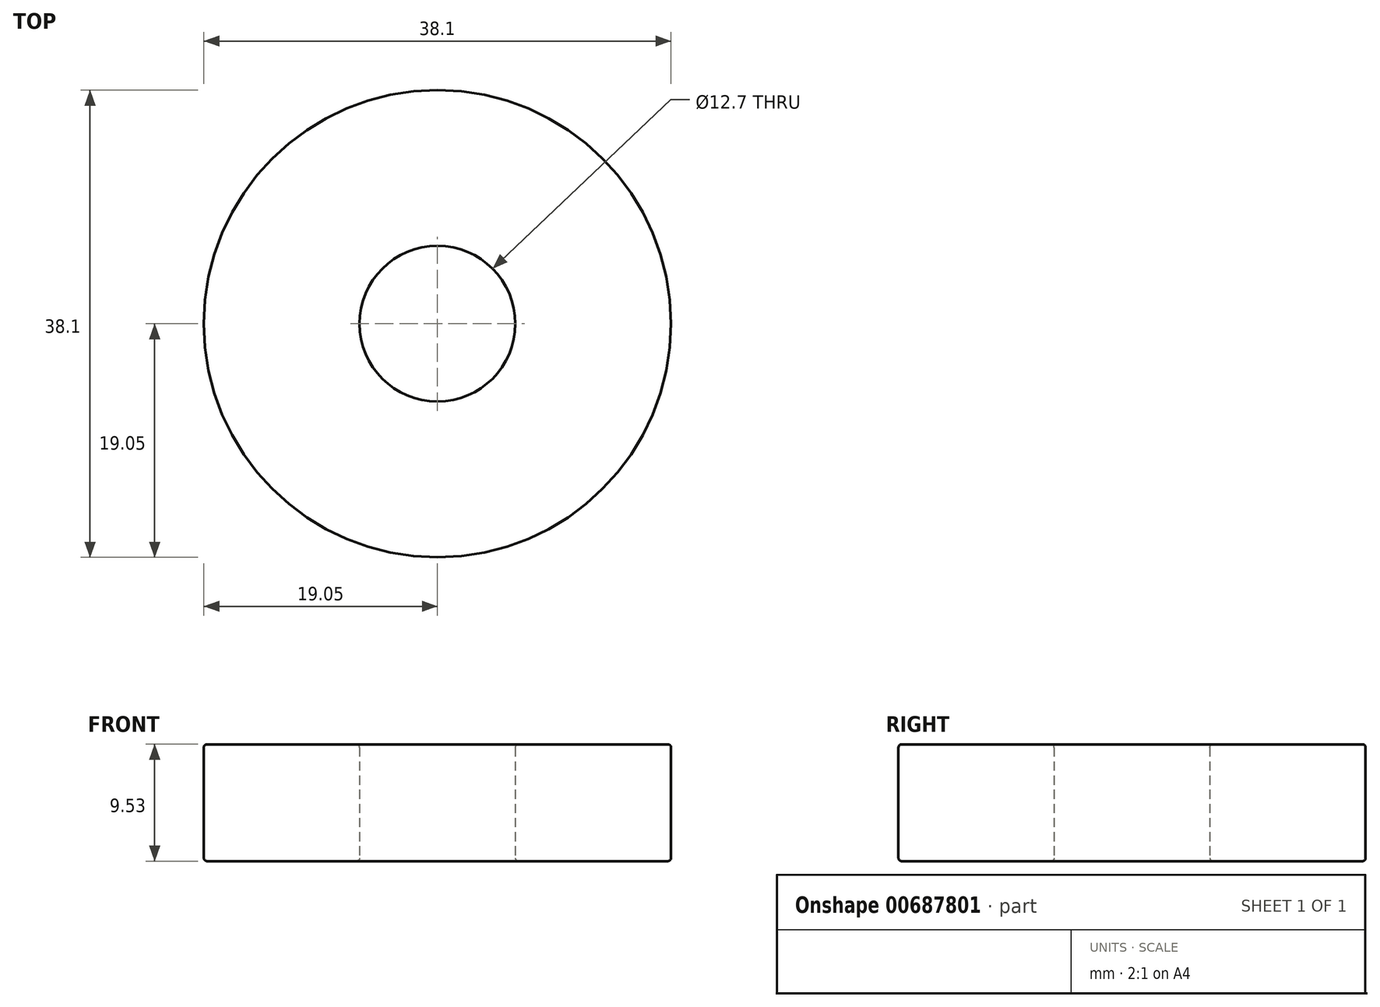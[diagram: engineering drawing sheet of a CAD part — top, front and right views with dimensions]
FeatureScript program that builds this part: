
annotation { "Feature Type Name" : "Feature", "Feature Type Description" : "" }
export const myFeature = defineFeature(function(context is Context, id is Id, definition is map)
    precondition{}
    {
        {
            var Q0;
            Q0=qCreatedBy(makeId("Top.planeOp"),FACE);
            var sketch = newSketch(context, id + "F0", { "sketchPlane" : qUnion([Q0])});
            skCircle(sketch, "E0", {"center": v(0, 0) * mm, "radius": 19.05 * mm});
            skCircle(sketch, "E1", {"center": v(0, 0) * mm, "radius": 6.35 * mm});
            skSolve(sketch);
        }
        {
            var Q0;
            Q0=qSketchRegion(id+"F0",true);
            extrude(context, id + "F1", {"entities" : qUnion([Q0]), "depth" : 9.52 * mm, "offsetDistance" : 25.4 * mm});
        }
        {
            var Q0;
            Q0=makeQuery(id+"F1.opExtrude","SWEPT_FACE",FACE,{"disambiguationData":[OSD([sQuery(id+"F0.wireOp",EDGE,"E0")])]});
            var Q1;
            Q1=makeQuery(id+"F1.opExtrude","SWEPT_FACE",FACE,{"disambiguationData":[OSD([sQuery(id+"F0.wireOp",EDGE,"E1")])]});
            fillet(context, id + "F2", {"entities" : qUnion([Q0, Q1]), "radius" : 0.25 * mm, "tangentPropagation" : true, "allowEdgeOverflow" : false});
        }
    });
